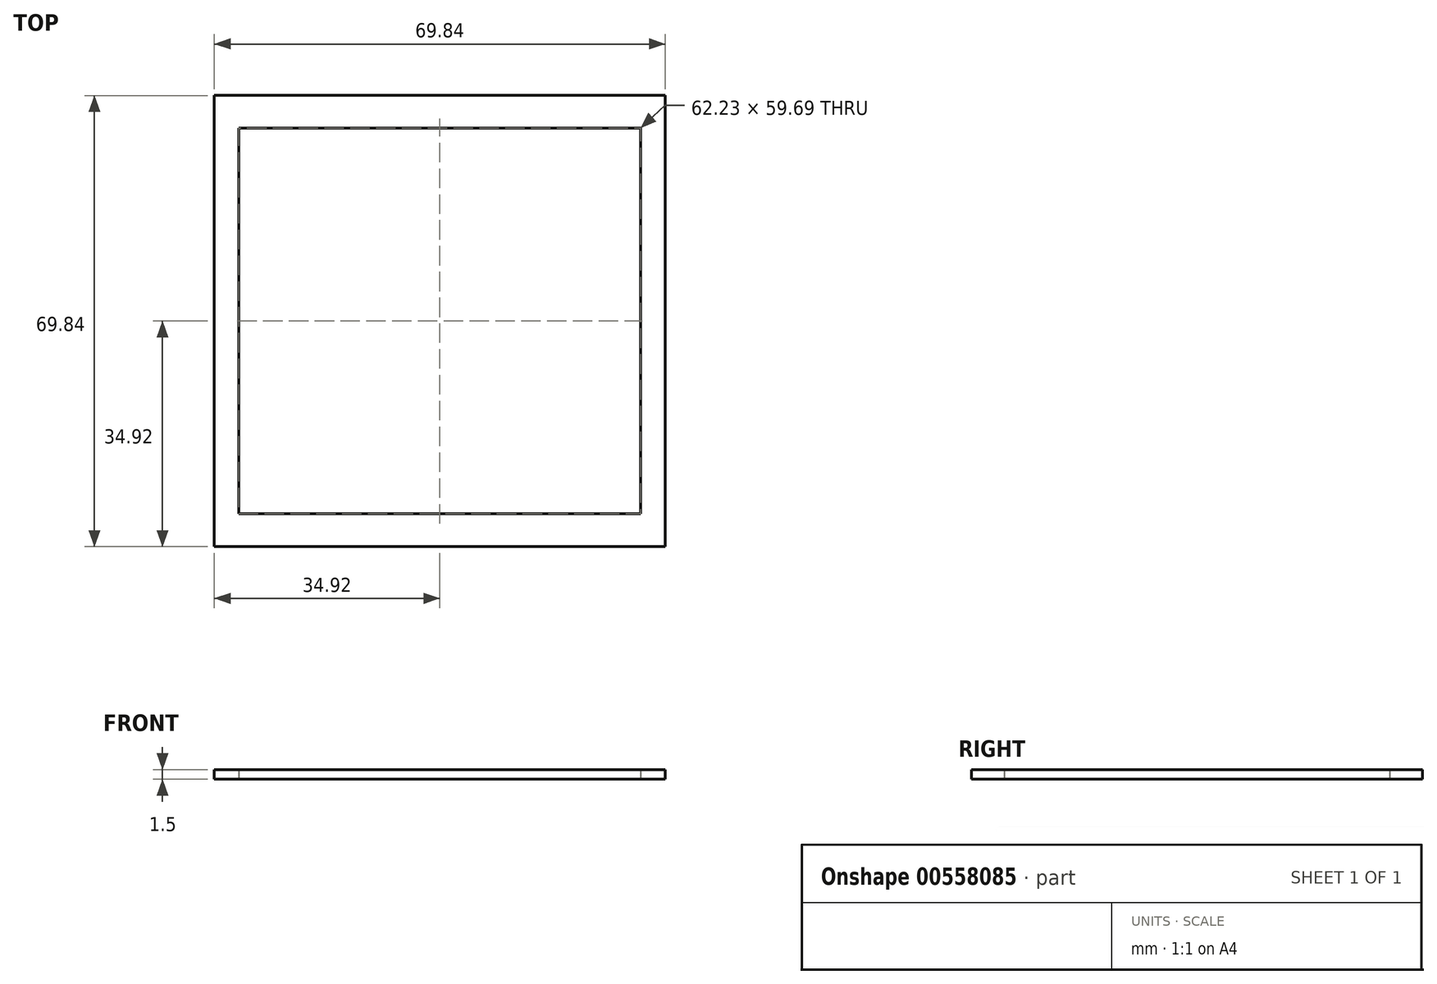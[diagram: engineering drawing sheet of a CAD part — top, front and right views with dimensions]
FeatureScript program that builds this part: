
annotation { "Feature Type Name" : "Feature", "Feature Type Description" : "" }
export const myFeature = defineFeature(function(context is Context, id is Id, definition is map)
    precondition{}
    {
        {
            var Q0;
            Q0=qCreatedBy(makeId("Top.planeOp"),FACE);
            var sketch = newSketch(context, id + "F0", { "sketchPlane" : qUnion([Q0])});
            skLineSegment(sketch, "E0.bottom", {"start": v(34.93, -34.92) * mm, "end": v(-34.93, -34.93) * mm});
            skLineSegment(sketch, "E0.top", {"start": v(34.92, 34.93) * mm, "end": v(-34.93, 34.92) * mm});
            skLineSegment(sketch, "E0.left", {"start": v(34.93, -34.92) * mm, "end": v(34.92, 34.93) * mm});
            skLineSegment(sketch, "E0.right", {"start": v(-34.93, -34.93) * mm, "end": v(-34.93, 34.92) * mm});
            skLineSegment(sketch, "E1.bottom", {"start": v(31.12, -29.85) * mm, "end": v(-31.11, -29.85) * mm});
            skLineSegment(sketch, "E1.top", {"start": v(31.12, 29.85) * mm, "end": v(-31.12, 29.85) * mm});
            skLineSegment(sketch, "E1.left", {"start": v(31.12, -29.85) * mm, "end": v(31.12, 29.85) * mm});
            skLineSegment(sketch, "E1.right", {"start": v(-31.11, -29.85) * mm, "end": v(-31.12, 29.85) * mm});
            skSolve(sketch);
        }
        {
            var Q0;
            Q0=makeQuery(id+"F0.imprint","IMPRINT",FACE,{"disambiguationData":[TD([[makeQuery(id+"F0.imprint","IMPRINT",EDGE,{"derivedFrom":sQuery(id+"F0.wireOp",EDGE,"E0.bottom")}),-1.0]])]});
            extrude(context, id + "F1", {"entities" : qUnion([Q0]), "depth" : 1.5 * mm, "offsetDistance" : 25 * mm});
        }
    });
